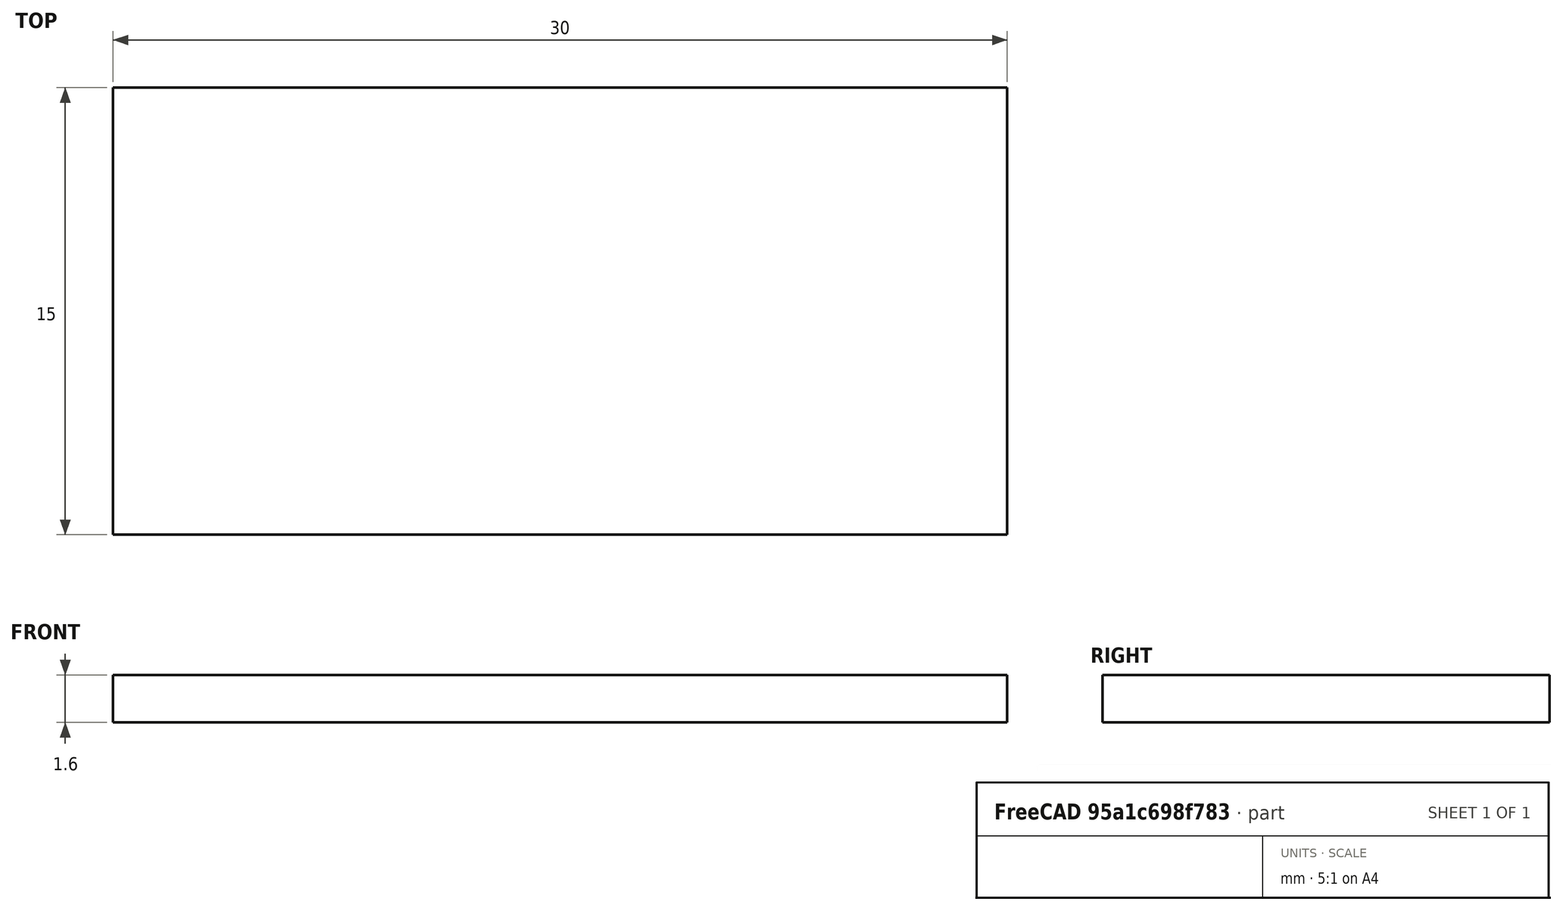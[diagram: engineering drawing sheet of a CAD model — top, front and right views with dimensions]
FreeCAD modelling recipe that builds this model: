
FCSTD DOCUMENT  (FreeCAD 0.19R24276 (Git))
Label: pir-baffel-screw-blocks
License: All rights reserved
LicenseURL: http://en.wikipedia.org/wiki/All_rights_reserved
objects: Sketcher::SketchObject×1, PartDesign::Pad×1, PartDesign::CoordinateSystem×1, PartDesign::Body×1
note: 5 computed .brp shape members not serialized (recipe doc carries the construction recipe); baked Part::Feature solids carry a one-line shape summary decoded from their .brp

FEATURE [Sketcher::SketchObject] Sketch
  FullyConstrained = true
  MapMode = 5
  Support = -> [XY_Plane]
  sketch-geometry (4):
    g0: LineSegment StartX=-15 StartY=7.5 StartZ=0 EndX=15 EndY=7.5 EndZ=0
    g1: LineSegment StartX=15 StartY=7.5 StartZ=0 EndX=15 EndY=-7.5 EndZ=0
    g2: LineSegment StartX=15 StartY=-7.5 StartZ=0 EndX=-15 EndY=-7.5 EndZ=0
    g3: LineSegment StartX=-15 StartY=-7.5 StartZ=0 EndX=-15 EndY=7.5 EndZ=0
  constraints (10):
    c: Coincident(g0,g1)
    c: Coincident(g1,g2)
    c: Coincident(g2,g3)
    c: Coincident(g3,g0)
    c: Horizontal(g2)
    c: Vertical(g1)
    c: DistanceX(g0,g0) = 30
    c: DistanceY(g3,g3) = 15
    c: Symmetric(g0,g2,g-1)
    c: Symmetric(g0,g0,g-2)
FEATURE [PartDesign::Pad] Pad  label="ScrewBlock"
  Direction = (1,1,1)
  Length = 1.6
  Length2 = 100
  Profile = -> Sketch
  Type = 0
FEATURE [PartDesign::CoordinateSystem] LCS_screwBlock
  AttacherType = Attacher::AttachEngine3D
  MapMode = 45
  Placement = pos=(2e-16,1e-16,1.6) rot=(0,0,1;1.5708rad)
  Support = -> [Pad]
FEATURE [PartDesign::Body] Body
  Group = -> [Sketch,Pad,LCS_screwBlock]
  Origin = -> Origin
  Tip = -> Pad
